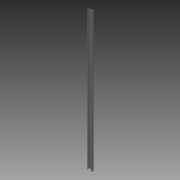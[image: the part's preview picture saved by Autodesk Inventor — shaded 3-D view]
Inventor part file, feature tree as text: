
AUTODESK INVENTOR PART (.ipt)
format: ipt  version: 2015 SP1 (Build 190203100, 203)  size: 115,200 bytes
history: native  units: in
note: dims shown in document units (in); Inventor stores cm internally (conversion verified against a paired STEP export)
features: extrude x1, sketch x1
ambient origin geometry x8: Origin, YZ Plane, XZ Plane, XY Plane, X Axis, Y Axis, Z Axis, Center Point
bodies: Solid1 (feature_tree)
feature tree (2):
  extrude  "Extrusion1"  Depth=60.0in
  sketch  "Sketch1"  dims[d0=2.0in d1=0.5in d2=0.5in d3=90.0deg d4=2.0in d5=90.0deg d6=0.5in d7=0.5in d8=0.25in d9=0.25in d10=0.25in d11=60.0deg d12=0.25in d13=60.0deg d14=150.0deg d15=150.0deg d16=0.25in d17=0.0625in d18=1.0625in d19=90.0deg d23=0.0625in d24=90.0deg d25=0.25in d26=0.0625in d27=90.0deg d28=0.03in d29=0.0625in d30=0.0312in d31=60.0in d32=0.0in]
